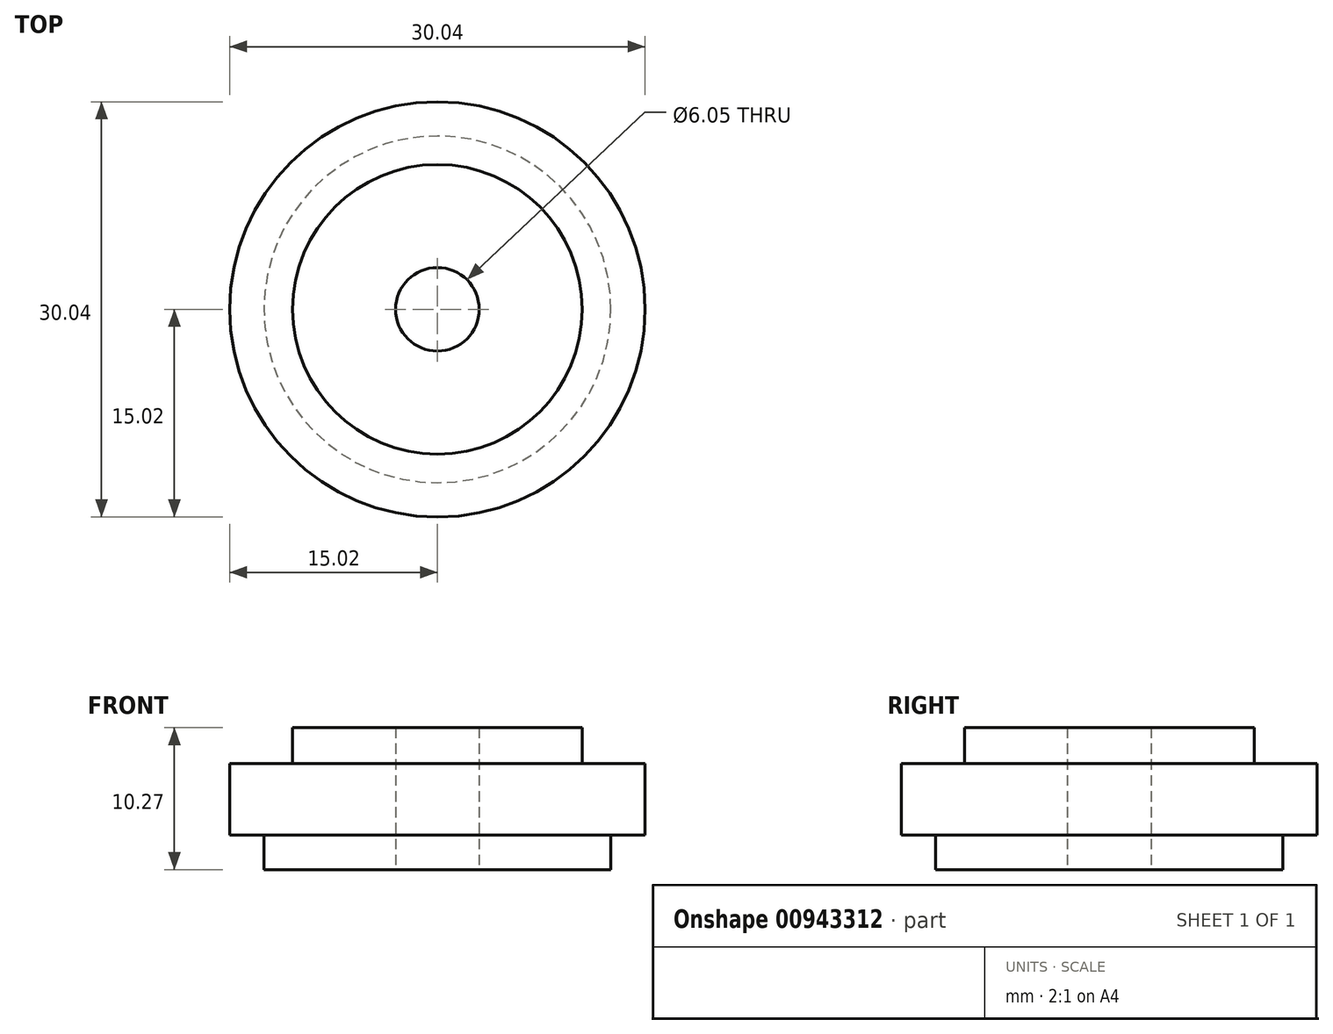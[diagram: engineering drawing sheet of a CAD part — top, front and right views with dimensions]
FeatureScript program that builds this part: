
annotation { "Feature Type Name" : "Feature", "Feature Type Description" : "" }
export const myFeature = defineFeature(function(context is Context, id is Id, definition is map)
    precondition{}
    {
        {
            var Q0;
            Q0=qCreatedBy(makeId("Top.planeOp"),FACE);
            var sketch = newSketch(context, id + "F0", { "sketchPlane" : qUnion([Q0])});
            skCircle(sketch, "E0", {"center": v(0, 0) * mm, "radius": 15.02 * mm});
            skCircle(sketch, "E1", {"center": v(0, 0) * mm, "radius": 12.55 * mm});
            skCircle(sketch, "E2", {"center": v(0, 0) * mm, "radius": 10.48 * mm});
            skSolve(sketch);
        }
        {
            var Q0;
            Q0=makeQuery(id+"F0.imprint","IMPRINT",FACE,{"disambiguationData":[TD([[makeQuery(id+"F0.imprint","IMPRINT",EDGE,{"derivedFrom":sQuery(id+"F0.wireOp",EDGE,"E2")}),1.0]])]});
            var Q1;
            Q1=makeQuery(id+"F0.imprint","IMPRINT",FACE,{"disambiguationData":[TD([[makeQuery(id+"F0.imprint","IMPRINT",EDGE,{"derivedFrom":sQuery(id+"F0.wireOp",EDGE,"NCLBZyI1-acK7-dJDt-KiFz-NdZ09yQW2BJR")}),1.0]])]});
            extrude(context, id + "F1", {"entities" : qUnion([Q0, Q1]), "depth" : 10.27 * mm, "offsetDistance" : 25.4 * mm});
        }
        {
            var Q0;
            Q0=makeQuery(id+"F0.imprint","IMPRINT",FACE,{"disambiguationData":[TD([[makeQuery(id+"F0.imprint","IMPRINT",EDGE,{"derivedFrom":sQuery(id+"F0.wireOp",EDGE,"E1")}),1.0]])]});
            extrude(context, id + "F2", {"entities" : qUnion([Q0]), "operationType" : NewBodyOperationType.ADD, "depth" : 7.67 * mm, "offsetDistance" : 25.4 * mm});
        }
        {
            var Q0;
            Q0=makeQuery(id+"F0.imprint","IMPRINT",FACE,{"disambiguationData":[TD([[makeQuery(id+"F0.imprint","IMPRINT",EDGE,{"derivedFrom":sQuery(id+"F0.wireOp",EDGE,"E0")}),1.0]])]});
            extrude(context, id + "F3", {"entities" : qUnion([Q0]), "operationType" : NewBodyOperationType.ADD, "depth" : 7.67 * mm, "offsetDistance" : 25.4 * mm, "hasSecondDirection" : true, "secondDirectionOppositeDirection" : false, "secondDirectionDepth" : 2.5 * mm});
        }
        {
            var Q0;
            Q0=sQuery(id+"F0.wireOp",VERTEX,"E0.center");
            var Q1;
            Q1=makeQuery(id+"F1.opExtrude","SWEPT_BODY",BODY,{"disambiguationData":[OSD([sQuery(id+"F0.wireOp",EDGE,"E2")])]});
            hole(context, id + "F4", {"style" : HoleStyle.SIMPLE, "endStyle" : HoleEndStyle.THROUGH, "oppositeDirection" : true, "standardTappedOrClearance" : lookupTablePath({ "fit" : "Loose (ASME)", "standard" : "ANSI", "size" : "#10", "type" : "Clearance" }), "standardBlindInLast" : lookupTablePath({ "fit" : "Loose", "standard" : "ANSI", "engagement" : "75%", "pitch" : "24 tpi", "size" : "#10", "type" : "Clearance & tapped" }), "holeDiameter" : 6.05 * mm, "majorDiameter" : 6.35 * mm, "isTappedThrough" : true, "tappedDepth" : 10.16 * mm, "tapClearance" : 3, "locations" : qUnion([Q0]), "scope" : qUnion([Q1])});
        }
    });
